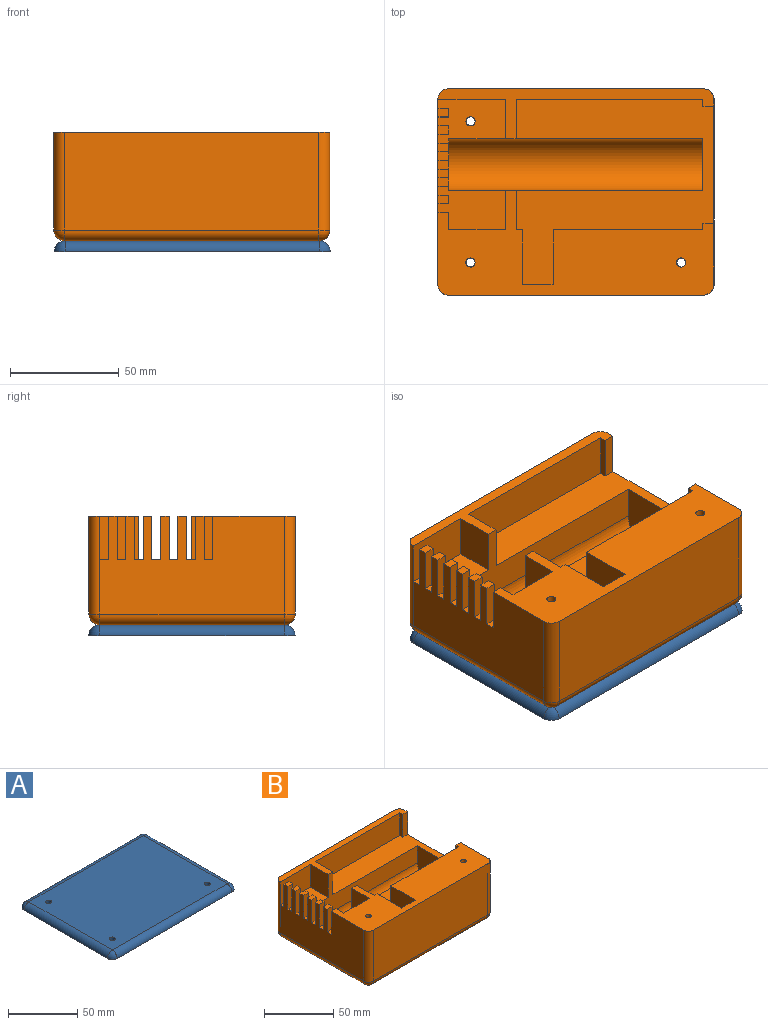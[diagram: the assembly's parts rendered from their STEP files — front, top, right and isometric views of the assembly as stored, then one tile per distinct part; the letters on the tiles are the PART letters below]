
ASSEMBLY  parts=2 mates=1
PART A: 13 faces, bbox 127x95x5 mm
  f0: plane 117x85mm, normal (0,0,1), area 9903.4mm2, adj f2,f3,f4,f6,f7,f10,f11
  f1: plane 127x95mm, normal (0,0,-1), area 12002mm2, adj f2,f3,f4,f5,f6,f7,f8,f9
  f2: cylinder r=2.1mm len=5mm, axis (0,0,1), area 66mm2, adj f0,f1
  f3: cylinder r=2.1mm len=5mm, axis (0,0,1), area 66mm2, adj f0,f1
  f4: cylinder r=2.1mm len=5mm, axis (0,0,1), area 66mm2, adj f0,f1
  f5: sphere r=5mm, area 39.3mm2, adj f1,f6,f7
  f6: cylinder r=5mm len=85mm, axis (0,-1,0), area 667.6mm2, adj f0,f1,f5,f8
  f7: cylinder r=5mm len=117mm, axis (-1,0,0), area 918.9mm2, adj f0,f1,f5,f9
  f8: sphere r=5mm, area 39.3mm2, adj f1,f6,f10
  f9: sphere r=5mm, area 39.3mm2, adj f1,f7,f11
  f10: cylinder r=5mm len=117mm, axis (1,0,0), area 918.9mm2, adj f0,f1,f8,f12
  f11: cylinder r=5mm len=85mm, axis (0,1,0), area 667.6mm2, adj f0,f1,f9,f12
  f12: sphere r=5mm, area 39.3mm2, adj f1,f10,f11
PART B: 92 faces, bbox 127x95x50 mm
  f0: plane 127x23mm, normal (0,0,1), area 729.3mm2, adj f16,f20,f23,f28,f29,f30,f31,f35
  f1: plane 5x4mm, normal (0,0,1), area 20mm2, adj f7,f8,f90,f91
  f2: plane 5x4mm, normal (0,0,1), area 20mm2, adj f7,f9,f88,f89
  f3: plane 5x4mm, normal (0,0,1), area 20mm2, adj f7,f11,f81,f87
  f4: plane 5x4mm, normal (0,0,1), area 20mm2, adj f7,f11,f78,f80
  f5: plane 5x4mm, normal (0,0,1), area 20mm2, adj f7,f11,f77,f86
  f6: plane 5x4mm, normal (0,0,1), area 20mm2, adj f7,f10,f84,f85
  f7: plane 85x45mm, normal (-1,0,0), area 3265mm2, adj f1,f2,f3,f4,f5,f6,f13,f18
  f8: plane 20x4mm, normal (1,0,0), area 80mm2, adj f1,f21,f90,f91
  f9: plane 20x4mm, normal (1,0,0), area 80mm2, adj f2,f21,f88,f89
  f10: plane 20x4mm, normal (1,0,0), area 80mm2, adj f6,f18,f84,f85
  f11: plane 47x24mm, normal (1,0,0), area 826.2mm2, adj f3,f4,f5,f18,f21,f23,f24,f25
  f12: plane 117x85mm, normal (0,0,-1), area 9810.3mm2, adj f40,f45,f46,f50,f53,f54,f55,f56
  f13: plane 127x48mm, normal (0,0,1), area 3566.6mm2, adj f7,f15,f16,f17,f19,f25,f26,f27
  f14: plane 27x24mm, normal (-1,0,0), area 586.2mm2, adj f22,f23,f24,f25
  f15: plane 20x3mm, normal (-1,0,0), area 60mm2, adj f13,f19,f22,f51
  f16: plane 85x45mm, normal (1,0,0), area 2745mm2, adj f0,f13,f22,f44,f47,f50,f51,f52
  f17: plane 20x3mm, normal (0,1,0), area 60mm2, adj f13,f22,f32,f37
  f18: plane 31x20mm, normal (0,0,1), area 508mm2, adj f7,f10,f11,f25,f26,f33,f34,f83
  f19: plane 69x20mm, normal (0,1,0), area 1380mm2, adj f13,f15,f22,f36
  f20: plane 86x20mm, normal (0,-1,0), area 1720mm2, adj f0,f22,f31,f35
  f21: plane 31x20mm, normal (0,0,1), area 514.1mm2, adj f7,f8,f9,f11,f23,f29,f30,f74
  f22: plane 91x85mm, normal (0,0,1), area 3716mm2, adj f14,f15,f16,f17,f19,f20,f23,f25
  f23: plane 117x35mm, normal (0,-1,0), area 1855mm2, adj f0,f11,f14,f21,f22,f24,f30,f31
  f24: cylinder r=12mm len=117mm, axis (-1,0,0), area 4410.8mm2, adj f11,f14,f23,f25
  f25: plane 117x35mm, normal (0,1,0), area 1855mm2, adj f11,f13,f14,f18,f22,f24,f32,f33
  f26: plane 26x20mm, normal (0,1,0), area 520mm2, adj f13,f18,f33,f34
  f27: plane 117x45mm, normal (0,-1,0), area 5265mm2, adj f13,f41,f46,f47
  f28: plane 117x45mm, normal (0,1,0), area 5265mm2, adj f0,f39,f44,f45
  f29: plane 31x20mm, normal (0,-1,0), area 620mm2, adj f0,f21,f30,f39
  f30: plane 20x18mm, normal (-1,0,0), area 360mm2, adj f0,f21,f23,f29
  f31: plane 20x18mm, normal (1,0,0), area 360mm2, adj f0,f20,f22,f23
  f32: plane 20x18mm, normal (1,0,0), area 360mm2, adj f13,f17,f22,f25
  f33: plane 20x18mm, normal (-1,0,0), area 360mm2, adj f13,f18,f25,f26
  f34: plane 20x8mm, normal (1,0,0), area 160mm2, adj f13,f18,f26,f83
  f35: plane 20x3mm, normal (-1,0,0), area 60mm2, adj f0,f20,f22,f52
  f36: plane 25x20mm, normal (-1,0,0), area 500mm2, adj f13,f19,f22,f38
  f37: plane 25x20mm, normal (1,0,0), area 500mm2, adj f13,f17,f22,f38
  f38: plane 20x14mm, normal (0,1,0), area 280mm2, adj f13,f22,f36,f37
  f39: cylinder r=5mm len=45mm, axis (0,0,-1), area 353.4mm2, adj f0,f7,f28,f29,f42
  f40: cylinder r=5mm len=85mm, axis (0,-1,0), area 667.6mm2, adj f7,f12,f42,f43
  f41: cylinder r=5mm len=45mm, axis (0,0,1), area 353.4mm2, adj f7,f13,f27,f43
  f42: sphere r=5mm, area 39.3mm2, adj f39,f40,f45
  f43: sphere r=5mm, area 39.3mm2, adj f40,f41,f46
  f44: cylinder r=5mm len=45mm, axis (0,0,-1), area 353.4mm2, adj f0,f16,f28,f48
  f45: cylinder r=5mm len=117mm, axis (1,0,0), area 918.9mm2, adj f12,f28,f42,f48
  f46: cylinder r=5mm len=117mm, axis (-1,0,0), area 918.9mm2, adj f12,f27,f43,f49
  f47: cylinder r=5mm len=45mm, axis (0,0,1), area 353.4mm2, adj f13,f16,f27,f49
  f48: sphere r=5mm, area 39.3mm2, adj f44,f45,f50
  f49: sphere r=5mm, area 39.3mm2, adj f46,f47,f50
  f50: cylinder r=5mm len=85mm, axis (0,-1,0), area 667.6mm2, adj f12,f16,f48,f49
  f51: plane 20x5mm, normal (0,1,0), area 100mm2, adj f13,f15,f16,f22
  f52: plane 20x5mm, normal (0,-1,0), area 100mm2, adj f0,f16,f22,f35
  f53: plane 20x3.6mm, normal (-0.87,-0.5,0), area 83.1mm2, adj f12,f54,f58,f59
  f54: plane 20x3.6mm, normal (-0.87,0.5,0), area 83.1mm2, adj f12,f53,f55,f59
  f55: plane 20x4.16mm, normal (0,1,0), area 83.1mm2, adj f12,f54,f56,f59
  f56: plane 20x3.6mm, normal (0.87,0.5,0), area 83.1mm2, adj f12,f55,f57,f59
  f57: plane 20x3.6mm, normal (0.87,-0.5,0), area 83.1mm2, adj f12,f56,f58,f59
  f58: plane 20x4.16mm, normal (0,-1,0), area 83.1mm2, adj f12,f53,f57,f59
  f59: plane 8.31x7.2mm, normal (0,0,-1), area 31mm2, adj f53,f54,f55,f56,f57,f58,f75
  f60: plane 20x3.6mm, normal (-0.87,-0.5,0), area 83.1mm2, adj f12,f61,f65,f66
  f61: plane 20x3.6mm, normal (-0.87,0.5,0), area 83.1mm2, adj f12,f60,f62,f66
  f62: plane 20x4.16mm, normal (0,1,0), area 83.1mm2, adj f12,f61,f63,f66
  f63: plane 20x3.6mm, normal (0.87,0.5,0), area 83.1mm2, adj f12,f62,f64,f66
  f64: plane 20x3.6mm, normal (0.87,-0.5,0), area 83.1mm2, adj f12,f63,f65,f66
  f65: plane 20x4.16mm, normal (0,-1,0), area 83.1mm2, adj f12,f60,f64,f66
  f66: plane 8.31x7.2mm, normal (0,0,-1), area 31mm2, adj f60,f61,f62,f63,f64,f65,f74
  f67: plane 20x3.6mm, normal (-0.87,-0.5,0), area 83.1mm2, adj f12,f68,f72,f73
  f68: plane 20x3.6mm, normal (-0.87,0.5,0), area 83.1mm2, adj f12,f67,f69,f73
  f69: plane 20x4.16mm, normal (0,1,0), area 83.1mm2, adj f12,f68,f70,f73
  f70: plane 20x3.6mm, normal (0.87,0.5,0), area 83.1mm2, adj f12,f69,f71,f73
  f71: plane 20x3.6mm, normal (0.87,-0.5,0), area 83.1mm2, adj f12,f70,f72,f73
  f72: plane 20x4.16mm, normal (0,-1,0), area 83.1mm2, adj f12,f67,f71,f73
  f73: plane 8.31x7.2mm, normal (0,0,-1), area 31mm2, adj f67,f68,f69,f70,f71,f72,f76
  f74: cylinder r=2.1mm len=10mm, axis (0,0,-1), area 131.9mm2, adj f21,f66
  f75: cylinder r=2.1mm len=30mm, axis (0,0,-1), area 395.8mm2, adj f13,f59
  f76: cylinder r=2.1mm len=30mm, axis (0,0,-1), area 395.8mm2, adj f13,f73
  f77: plane 20x5mm, normal (0,1,0), area 100mm2, adj f5,f7,f11,f79
  f78: plane 20x5mm, normal (0,-1,0), area 100mm2, adj f4,f7,f11,f79
  f79: plane 5x4mm, normal (0,0,1), area 20mm2, adj f7,f11,f77,f78
  f80: plane 20x5mm, normal (0,1,0), area 100mm2, adj f4,f7,f11,f82
  f81: plane 20x5mm, normal (0,-1,0), area 100mm2, adj f3,f7,f11,f82
  f82: plane 5x4mm, normal (0,0,1), area 20mm2, adj f7,f11,f80,f81
  f83: plane 20x5mm, normal (0,1,0), area 100mm2, adj f7,f13,f18,f34
  f84: plane 20x5mm, normal (0,-1,0), area 100mm2, adj f6,f7,f10,f18
  f85: plane 20x5mm, normal (0,1,0), area 100mm2, adj f6,f7,f10,f18
  f86: plane 20x5mm, normal (0,-1,0), area 100mm2, adj f5,f7,f11,f18
  f87: plane 20x5mm, normal (0,1,0), area 100mm2, adj f3,f7,f11,f21
  f88: plane 20x5mm, normal (0,-1,0), area 100mm2, adj f2,f7,f9,f21
  f89: plane 20x5mm, normal (0,1,0), area 100mm2, adj f2,f7,f9,f21
  f90: plane 20x5mm, normal (0,-1,0), area 100mm2, adj f1,f7,f8,f21
  f91: plane 20x5mm, normal (0,1,0), area 100mm2, adj f1,f7,f8,f21
PLACE A t=(57.12,-11.33,-20)mm
PLACE B t=(0,1,0)mm
MATE slider A.f0 <-> B.f12  axis (0,0,1) through (58.72,-11.35,-15)mm
